# Revit family: GRAS_HW-19NW-20-30 HS (W)
name_source: partatom
category: Osprzęt hydrauliczny
revit_build: Autodesk Revit 2018 (Build: 20190510_1515(x64)
units: mm (PartAtom-declared; Revit-internal decimal feet)

## family parameters
Obiekt nadrzędny = Powierzchnia
Punkt obliczania pomieszczeń = Nie
Tnij formami wycięć po wczytaniu = Nie
Typ części = Normalny
Współdzielony = Nie
Wymiar okrągłego złącza = Użyj średnicy

## types (2) — shared parameters
Cabinet_Depth = 220 mm  [stored 0.721785 ft]
Cabinet_Height = 795 mm  [stored 2.60827 ft]
Cabinet_Width = 795 mm  [stored 2.60827 ft]
D1 = 90 mm  [stored 0.295276 ft]
DN = 19 mm  [stored 0.062336 ft]
Flow = 35.0 L/s
H1 = 90 mm  [stored 0.295276 ft]
Hole_Depth = 230 mm
Hole_Height = 815 mm
Hole_Width = 815 mm
K_factor = 42
Model = HW-19NW-20/30 HS (W), RAL3000
Opis = http://gras.pl
Producent = GRAS PPPH
URL = http://www.gras.pl
W1 = 90 mm  [stored 0.295276 ft]
picH = 60 mm  [stored 0.19685 ft]
zero-valued in all types: Domyślna rzędna, mounting_plane, zer0

## per-type parameters (varying)
| type | Cabinet_Material |
| HW-19NW-20/30 HS (W), RAL9010 | DC01, RAL9010 |
| HW-19NW-20/30 HS (W), RAL3000 | DC01, RAL3000 |

note: [stored X ft] marks values corroborated as IEEE doubles in the binary element streams (Revit-internal decimal feet)

## geometry (parser evidence)
native form markers: Blend x8
no freeform markers — native parametric forms only
